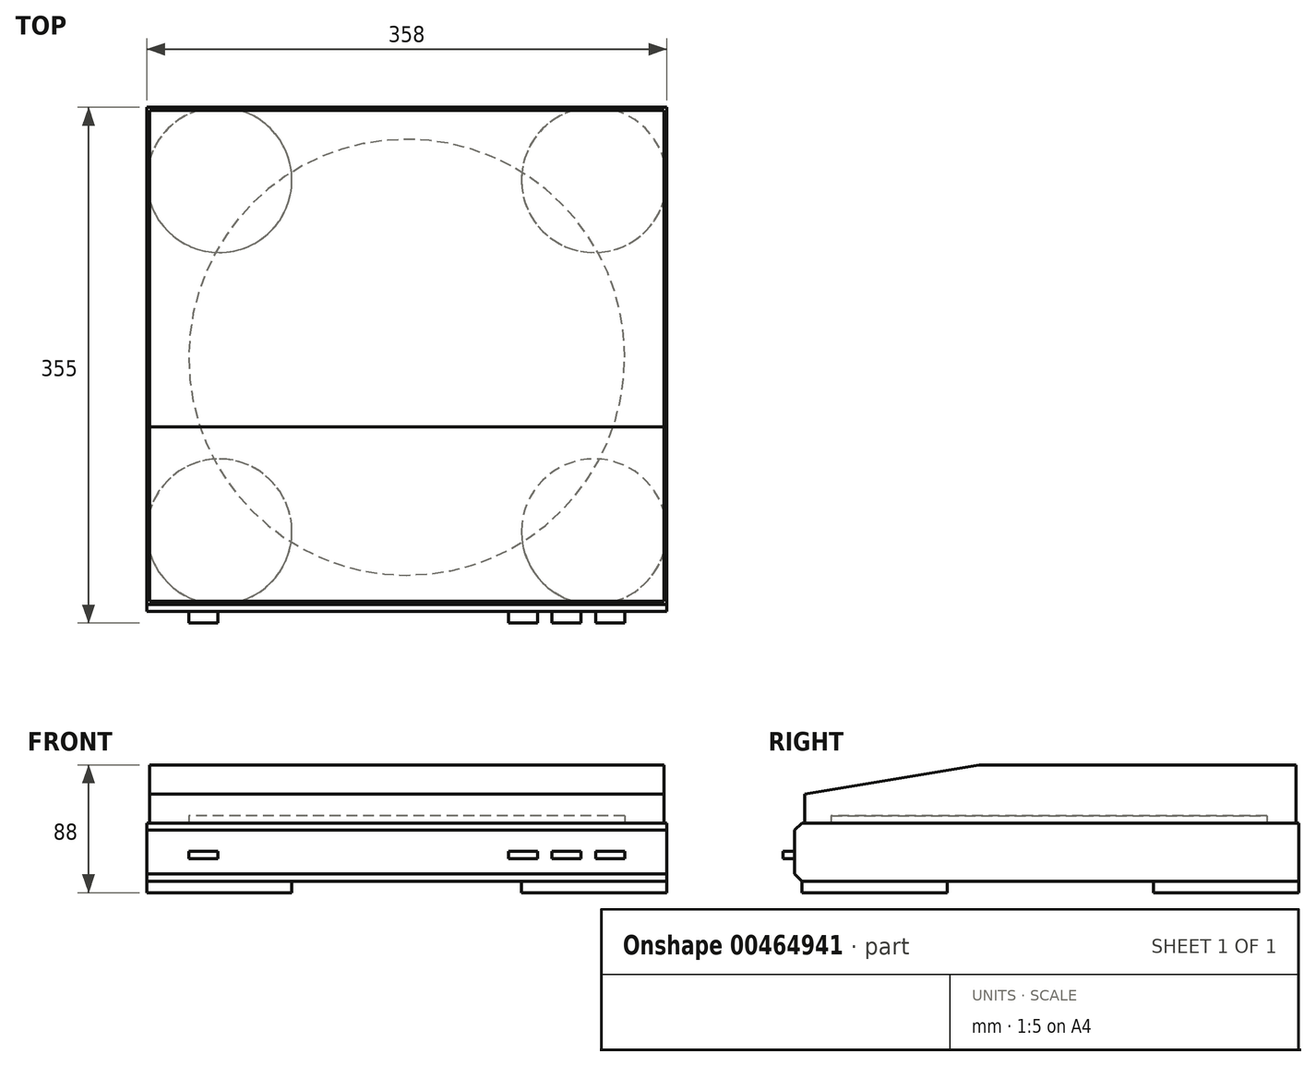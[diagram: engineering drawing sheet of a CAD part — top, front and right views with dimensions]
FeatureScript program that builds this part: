
annotation { "Feature Type Name" : "Feature", "Feature Type Description" : "" }
export const myFeature = defineFeature(function(context is Context, id is Id, definition is map)
    precondition{}
    {
        {
            var Q0;
            Q0=qCreatedBy(makeId("Right.planeOp"),FACE);
            var sketch = newSketch(context, id + "F0", { "sketchPlane" : qUnion([Q0])});
            skLineSegment(sketch, "E0.bottom", {"start": v(0, 0) * mm, "end": v(347, 0) * mm});
            skLineSegment(sketch, "E0.top", {"start": v(0, 40) * mm, "end": v(347, 40) * mm});
            skLineSegment(sketch, "E0.left", {"start": v(0, 0) * mm, "end": v(0, 40) * mm});
            skLineSegment(sketch, "E0.right", {"start": v(347, 0) * mm, "end": v(347, 40) * mm});
            skSolve(sketch);
        }
        {
            var Q0;
            Q0 = qSketchRegion(id + "F0", true);
            extrude(context, id + "F1", {"entities" : qUnion([Q0]), "endBound" : BoundingType.SYMMETRIC, "depth" : 358 * mm, "hasSecondDirection" : true, "secondDirectionOppositeDirection" : true, "secondDirectionDepth" : 25 * mm});
        }
        {
            var Q0;
            Q0=makeQuery(id+"F1.opExtrude","SWEPT_EDGE",EDGE,{"disambiguationData":[OSD([sQuery(id+"F0.wireOp",EDGE,"E0.top"),sQuery(id+"F0.wireOp",EDGE,"E0.left")])]});
            var Q1;
            Q1=makeQuery(id+"F1.opExtrude","SWEPT_EDGE",EDGE,{"disambiguationData":[OSD([sQuery(id+"F0.wireOp",EDGE,"E0.bottom"),sQuery(id+"F0.wireOp",EDGE,"E0.left")])]});
            chamfer(context, id + "F2", {"entities" : qUnion([Q0, Q1]), "width" : 5 * mm, "tangentPropagation" : true});
        }
        {
            var Q0;
            Q0=makeQuery(id+"F1.opExtrude","SWEPT_FACE",FACE,{"disambiguationData":[OSD([sQuery(id+"F0.wireOp",EDGE,"E0.left")])]});
            var sketch = newSketch(context, id + "F3", { "sketchPlane" : qUnion([Q0])});
            skLineSegment(sketch, "E1.bottom", {"start": v(-130, 15.5) * mm, "end": v(-150, 15.5) * mm});
            skLineSegment(sketch, "E1.top", {"start": v(-130, 20.5) * mm, "end": v(-150, 20.5) * mm});
            skLineSegment(sketch, "E1.left", {"start": v(-130, 15.5) * mm, "end": v(-130, 20.5) * mm});
            skLineSegment(sketch, "E1.right", {"start": v(-150, 15.5) * mm, "end": v(-150, 20.5) * mm});
            skPoint(sketch, "E1.middle", {"position": v(-140, 18) * mm});
            skLineSegment(sketch, "E2.bottom", {"start": v(120, 15.5) * mm, "end": v(100, 15.5) * mm});
            skLineSegment(sketch, "E2.top", {"start": v(120, 20.5) * mm, "end": v(100, 20.5) * mm});
            skLineSegment(sketch, "E2.left", {"start": v(120, 15.5) * mm, "end": v(120, 20.5) * mm});
            skLineSegment(sketch, "E2.right", {"start": v(100, 15.5) * mm, "end": v(100, 20.5) * mm});
            skPoint(sketch, "E2.middle", {"position": v(110, 18) * mm});
            skLineSegment(sketch, "E3.bottom", {"start": v(150, 15.5) * mm, "end": v(130, 15.5) * mm});
            skLineSegment(sketch, "E3.top", {"start": v(150, 20.5) * mm, "end": v(130, 20.5) * mm});
            skLineSegment(sketch, "E3.left", {"start": v(150, 15.5) * mm, "end": v(150, 20.5) * mm});
            skLineSegment(sketch, "E3.right", {"start": v(130, 15.5) * mm, "end": v(130, 20.5) * mm});
            skPoint(sketch, "E3.middle", {"position": v(140, 18) * mm});
            skLineSegment(sketch, "E4.bottom", {"start": v(90, 15.5) * mm, "end": v(70, 15.5) * mm});
            skLineSegment(sketch, "E4.top", {"start": v(90, 20.5) * mm, "end": v(70, 20.5) * mm});
            skLineSegment(sketch, "E4.left", {"start": v(90, 15.5) * mm, "end": v(90, 20.5) * mm});
            skLineSegment(sketch, "E4.right", {"start": v(70, 15.5) * mm, "end": v(70, 20.5) * mm});
            skPoint(sketch, "E4.middle", {"position": v(80, 18) * mm});
            skSolve(sketch);
        }
        {
            var Q0;
            Q0 = qSketchRegion(id + "F3", true);
            extrude(context, id + "F4", {"entities" : qUnion([Q0]), "operationType" : NewBodyOperationType.ADD, "depth" : 8 * mm});
        }
        {
            var Q0;
            Q0=makeQuery(id+"F1.opExtrude","SWEPT_FACE",FACE,{"disambiguationData":[OSD([sQuery(id+"F0.wireOp",EDGE,"E0.top")])]});
            var sketch = newSketch(context, id + "F5", { "sketchPlane" : qUnion([Q0])});
            skCircle(sketch, "E5", {"center": v(0, 175) * mm, "radius": 150 * mm});
            skSolve(sketch);
        }
        {
            var Q0;
            Q0 = qSketchRegion(id + "F5", true);
            extrude(context, id + "F6", {"entities" : qUnion([Q0]), "operationType" : NewBodyOperationType.ADD, "depth" : 5 * mm});
        }
        {
            var Q0;
            Q0=qCreatedBy(makeId("Right.planeOp"),FACE);
            var sketch = newSketch(context, id + "F7", { "sketchPlane" : qUnion([Q0])});
            skLineSegment(sketch, "E6.bottom", {"start": v(345, 40) * mm, "end": v(7, 40) * mm});
            skLineSegment(sketch, "E6.top", {"start": v(345, 80) * mm, "end": v(127, 80) * mm});
            skLineSegment(sketch, "E6.left", {"start": v(345, 40) * mm, "end": v(345, 80) * mm});
            skLineSegment(sketch, "E6.right", {"start": v(7, 40) * mm, "end": v(7, 60) * mm});
            skLineSegment(sketch, "E7", {"start": v(7, 60) * mm, "end": v(127, 80) * mm});
            skPoint(sketch, "E8.orphan", {"position": v(7, 80) * mm});
            skSolve(sketch);
        }
        {
            var Q0;
            Q0 = qSketchRegion(id + "F7", true);
            extrude(context, id + "F8", {"entities" : qUnion([Q0]), "endBound" : BoundingType.SYMMETRIC, "depth" : (358 - 4) * mm});
        }
        {
            var Q0;
            Q0=makeQuery(id+"F1.opExtrude","SWEPT_FACE",FACE,{"disambiguationData":[OSD([sQuery(id+"F0.wireOp",EDGE,"E0.bottom")])]});
            var sketch = newSketch(context, id + "F9", { "sketchPlane" : qUnion([Q0])});
            skLineSegment(sketch, "E9.bottom", {"start": v(129, -55) * mm, "end": v(-129, -55) * mm, "construction": true});
            skLineSegment(sketch, "E9.top", {"start": v(129, -297) * mm, "end": v(-129, -297) * mm, "construction": true});
            skLineSegment(sketch, "E9.left", {"start": v(129, -55) * mm, "end": v(129, -297) * mm, "construction": true});
            skLineSegment(sketch, "E9.right", {"start": v(-129, -55) * mm, "end": v(-129, -297) * mm, "construction": true});
            skCircle(sketch, "E10", {"center": v(129, -55) * mm, "radius": 50 * mm});
            skCircle(sketch, "E11", {"center": v(-129, -55) * mm, "radius": 50 * mm});
            skCircle(sketch, "E12", {"center": v(-129, -297) * mm, "radius": 50 * mm});
            skCircle(sketch, "E13", {"center": v(129, -297) * mm, "radius": 50 * mm});
            skSolve(sketch);
        }
        {
            var Q0;
            Q0 = qSketchRegion(id + "F9", true);
            extrude(context, id + "F10", {"entities" : qUnion([Q0]), "operationType" : NewBodyOperationType.ADD, "depth" : 8 * mm});
        }
    });
